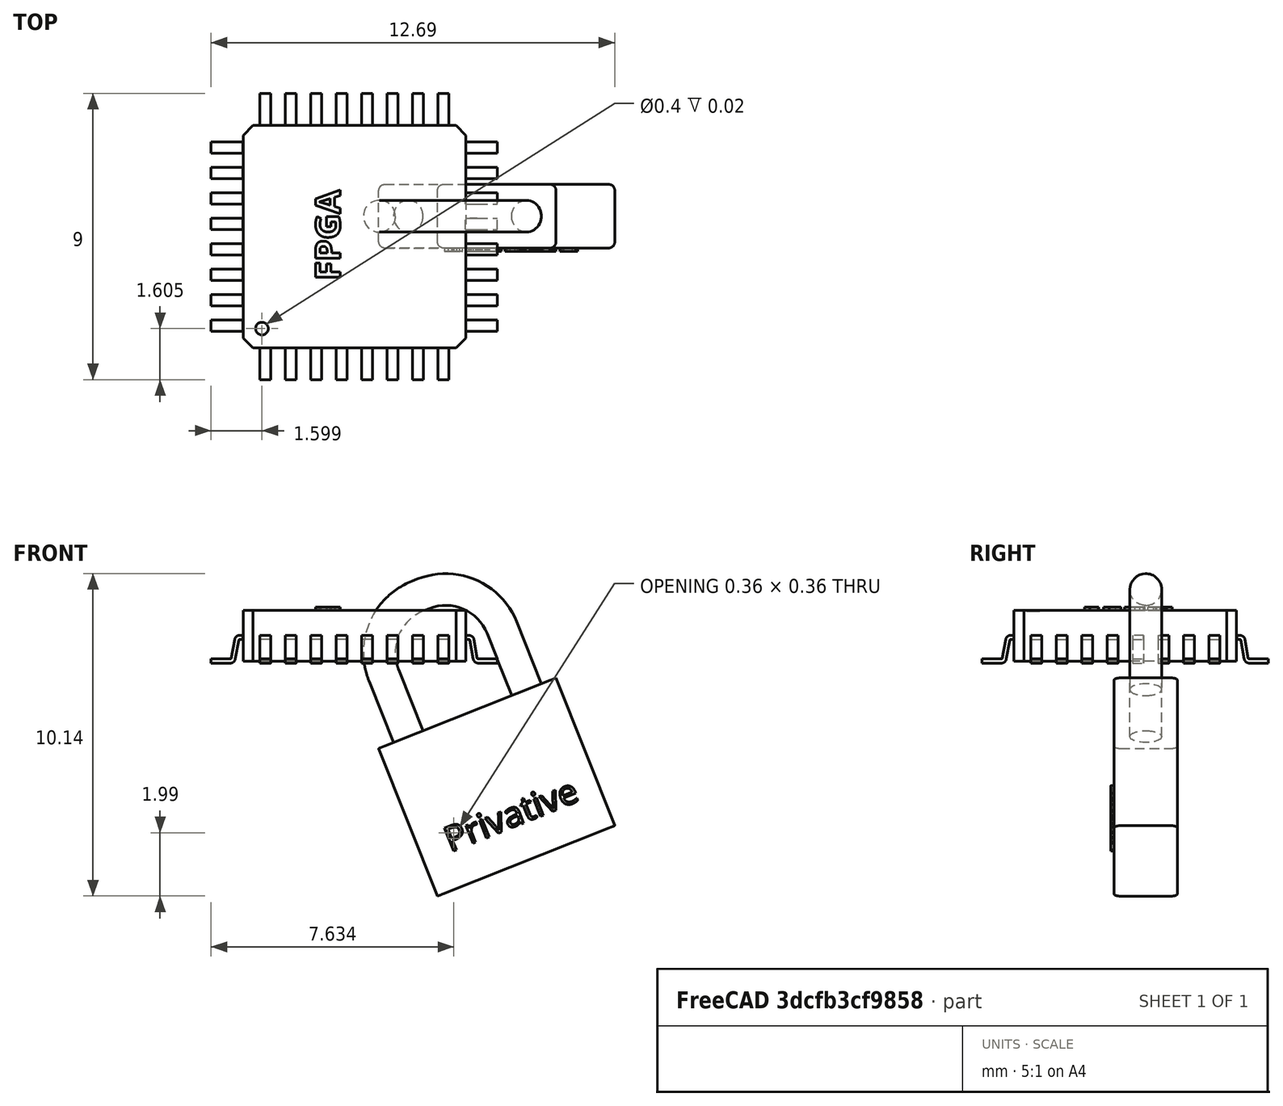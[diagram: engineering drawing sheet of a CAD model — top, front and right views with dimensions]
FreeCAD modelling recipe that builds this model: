
FCSTD DOCUMENT  (FreeCAD 0.16R6703 (Git))
Label: fpga-privative-1
License: CC-BY 3.0
LicenseURL: http://creativecommons.org/licenses/by/3.0/
objects: Part::Part2DObjectPython×5, Part::Extrusion×3, Part::Compound×1, Part::Sweep×1
note: 10 computed .brp shape members not serialized (recipe doc carries the construction recipe); baked Part::Feature solids carry a one-line shape summary decoded from their .brp

FEATURE [Part::Compound] Compound020  label="PQFP-034"
  Placement = pos=(-5.71099,-9.13488,1.7) rot=(0,0,1;0rad)
FEATURE [Part::Part2DObjectPython] DWire  # Draft 2D object (typed FeaturePython)
  ChamferSize = 0
  Closed = false
  End = (2,0,0)
  FilletRadius = 1.9
  Length = 10.369
  MakeFace = true
  Points = (5) [(-2,0,-1.22465e-16),(-2,0,2),(-2,0,4),(2,0,4),(2,0,1.22465e-16)]
  Start = (-2,0,0)
  Subdivisions = 0
FEATURE [Part::Part2DObjectPython] Circle  # Draft 2D object (typed FeaturePython)
  FirstAngle = 0
  LastAngle = 0
  MakeFace = true
  Placement = pos=(-2,0,0) rot=(0,0,1;0rad)
  Radius = 0.5
FEATURE [Part::Sweep] Sweep
  Frenet = true
  Placement = pos=(2.36927,-4,0.070678) rot=(0,-1,0;0.378224rad)
  Sections = -> [Circle]
  Solid = true
  Spine = -> DWire
  Transition = 1
FEATURE [Part::Part2DObjectPython] Rectangle  # Draft 2D object (typed FeaturePython)
  ChamferSize = 0
  Columns = 1
  FilletRadius = 0.2
  Height = -2
  Length = 6
  MakeFace = true
  Placement = pos=(-3,1,0) rot=(0,0,1;0rad)
  Rows = 1
FEATURE [Part::Extrusion] Extrude
  Base = -> Rectangle
  Dir = (0,0,-5)
  Placement = pos=(2.36927,-4,0.070678) rot=(0,-1,0;0.378224rad)
  Solid = true
FEATURE [Part::Part2DObjectPython] ShapeString  # Draft 2D object (typed FeaturePython)
  FontFile = <userpath>/develop/fpgawars.github.io/images/src/Open_Sans/OpenSans-Bold.ttf
  Placement = pos=(-9.34532,3.35513,3.3) rot=(0,0,1;0rad)
  Size = 1
  String = FPGA
  Tracking = 0
FEATURE [Part::Extrusion] Extrude001
  Base = -> ShapeString
  Dir = (0,0,0.1)
  Placement = pos=(1.72771,3.32716,0) rot=(0,0,1;1.5708rad)
  Solid = true
FEATURE [Part::Part2DObjectPython] ShapeString001  # Draft 2D object (typed FeaturePython)
  FontFile = <userpath>/develop/fpgawars.github.io/images/src/Open_Sans/OpenSans-Regular.ttf
  Placement = pos=(1.83581,-5,-4.30397) rot=(0.965264,-0.184751,0.184751;1.60614rad)
  Size = 1
  String = Privative
  Support = -> Extrude
  Tracking = 0
FEATURE [Part::Extrusion] Extrude002
  Base = -> ShapeString001
  Dir = (0,-0.1,0)
  Solid = true
